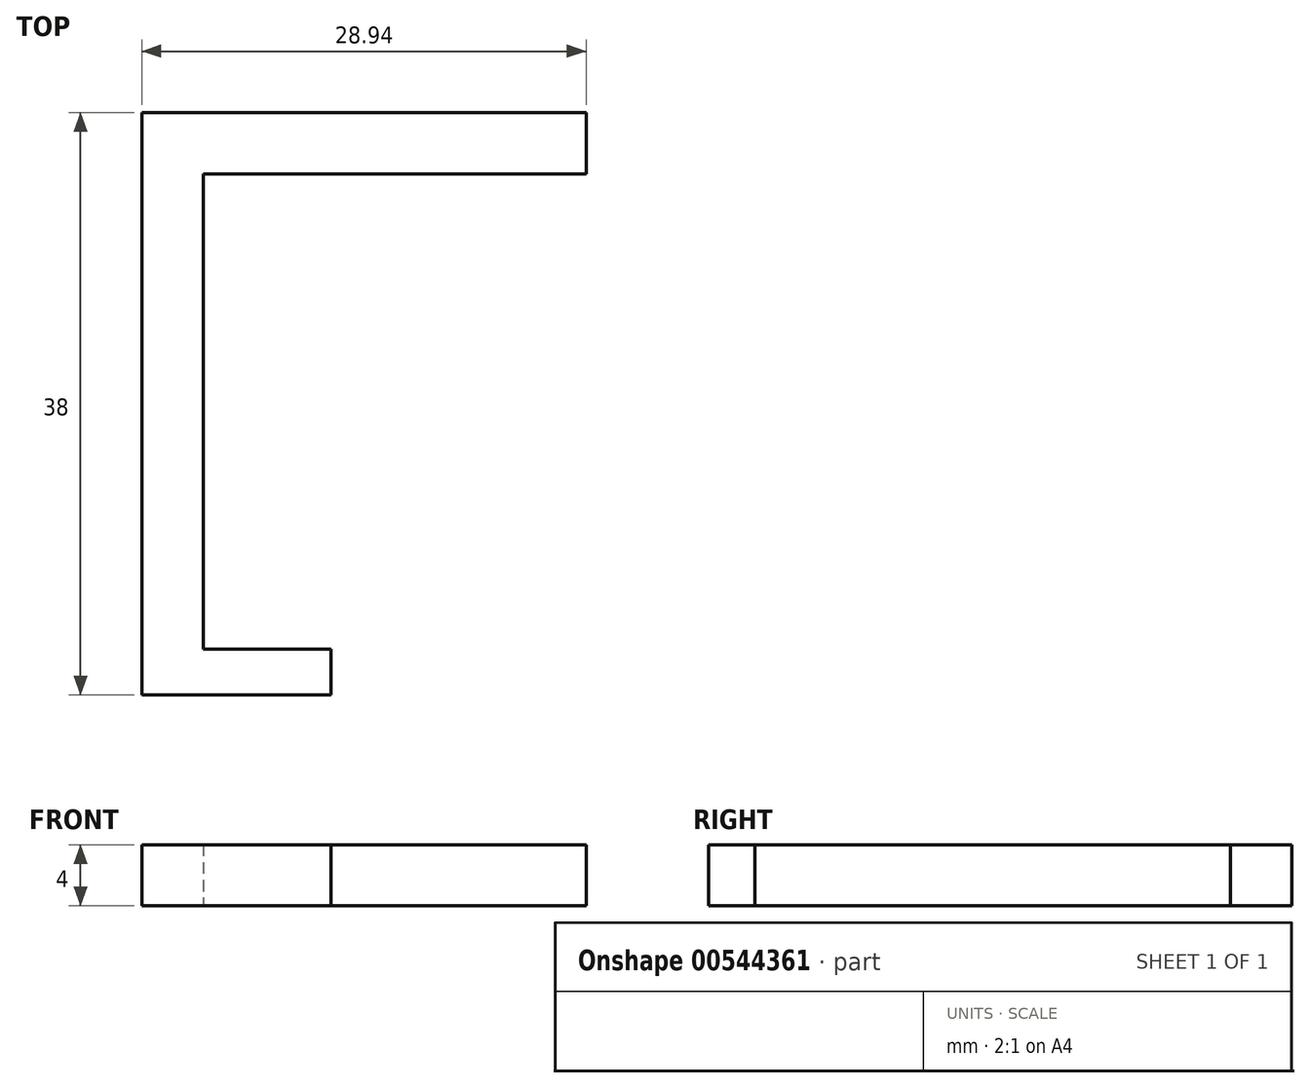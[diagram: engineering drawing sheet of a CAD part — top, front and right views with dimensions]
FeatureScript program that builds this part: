
annotation { "Feature Type Name" : "Feature", "Feature Type Description" : "" }
export const myFeature = defineFeature(function(context is Context, id is Id, definition is map)
    precondition{}
    {
        {
            var Q0;
            Q0=qCreatedBy(makeId("Top.planeOp"),FACE);
            var sketch = newSketch(context, id + "F0", { "sketchPlane" : qUnion([Q0])});
            skLineSegment(sketch, "E0.bottom", {"start": v(-23.8, 31.56) * mm, "end": v(-19.8, 31.56) * mm});
            skLineSegment(sketch, "E0.top", {"start": v(-23.8, -6.44) * mm, "end": v(-19.8, -6.44) * mm});
            skLineSegment(sketch, "E0.left", {"start": v(-23.8, 31.56) * mm, "end": v(-23.8, -6.44) * mm});
            skLineSegment(sketch, "E0.right", {"start": v(-19.8, 31.56) * mm, "end": v(-19.8, -6.44) * mm});
            skLineSegment(sketch, "E1.bottom", {"start": v(-19.8, 31.56) * mm, "end": v(5.13, 31.56) * mm});
            skLineSegment(sketch, "E1.top", {"start": v(-19.8, 27.56) * mm, "end": v(5.13, 27.56) * mm});
            skLineSegment(sketch, "E1.left", {"start": v(-19.8, 31.56) * mm, "end": v(-19.8, 27.56) * mm});
            skLineSegment(sketch, "E1.right", {"start": v(5.13, 31.56) * mm, "end": v(5.13, 27.56) * mm});
            skLineSegment(sketch, "E2.bottom", {"start": v(-19.8, -6.44) * mm, "end": v(-11.48, -6.44) * mm});
            skLineSegment(sketch, "E2.top", {"start": v(-19.8, -3.44) * mm, "end": v(-11.48, -3.44) * mm});
            skLineSegment(sketch, "E2.left", {"start": v(-19.8, -6.44) * mm, "end": v(-19.8, -3.44) * mm});
            skLineSegment(sketch, "E2.right", {"start": v(-11.48, -6.44) * mm, "end": v(-11.48, -3.44) * mm});
            skSolve(sketch);
        }
        {
            var Q0;
            Q0 = qSketchRegion(id + "F0", true);
            extrude(context, id + "F1", {"entities" : qUnion([Q0]), "depth" : 4 * mm, "offsetDistance" : 25 * mm});
        }
        {
            var Q0;
            Q0=makeQuery(id+"F1.opExtrude","CAP_FACE",FACE,{"disambiguationData":[OSD([sQuery(id+"F0.wireOp",EDGE,"E0.bottom"),sQuery(id+"F0.wireOp",EDGE,"E0.top"),sQuery(id+"F0.wireOp",EDGE,"E0.left"),sQuery(id+"F0.wireOp",EDGE,"E0.right"),sQuery(id+"F0.wireOp",EDGE,"E1.bottom"),sQuery(id+"F0.wireOp",EDGE,"E1.top"),sQuery(id+"F0.wireOp",EDGE,"E1.right"),sQuery(id+"F0.wireOp",EDGE,"E2.bottom"),sQuery(id+"F0.wireOp",EDGE,"E2.top"),sQuery(id+"F0.wireOp",EDGE,"E2.right")])],"isStart":false});
            var sketch = newSketch(context, id + "F2", { "sketchPlane" : qUnion([Q0])});
            skLineSegment(sketch, "E3", {"start": v(-11.48, -3.44) * mm, "end": v(-19.8, -3.44) * mm});
            skLineSegment(sketch, "E4", {"start": v(-19.8, -3.44) * mm, "end": v(-19.8, 27.56) * mm});
            skLineSegment(sketch, "E5", {"start": v(-19.8, 27.56) * mm, "end": v(5.13, 27.56) * mm});
            skSolve(sketch);
        }
        {
            var Q0;
            Q0=sQuery(id+"F2.wireOp",EDGE,"E4");
            var Q1;
            Q1=sQuery(id+"F2.wireOp",EDGE,"E5");
            var Q2;
            Q2=sQuery(id+"F2.wireOp",EDGE,"E3");
            extrude(context, id + "F3", {"bodyType" : ToolBodyType.SURFACE, "surfaceEntities" : qUnion([Q0, Q1, Q2]), "depth" : 65 * mm, "offsetDistance" : 25 * mm});
        }
    });
